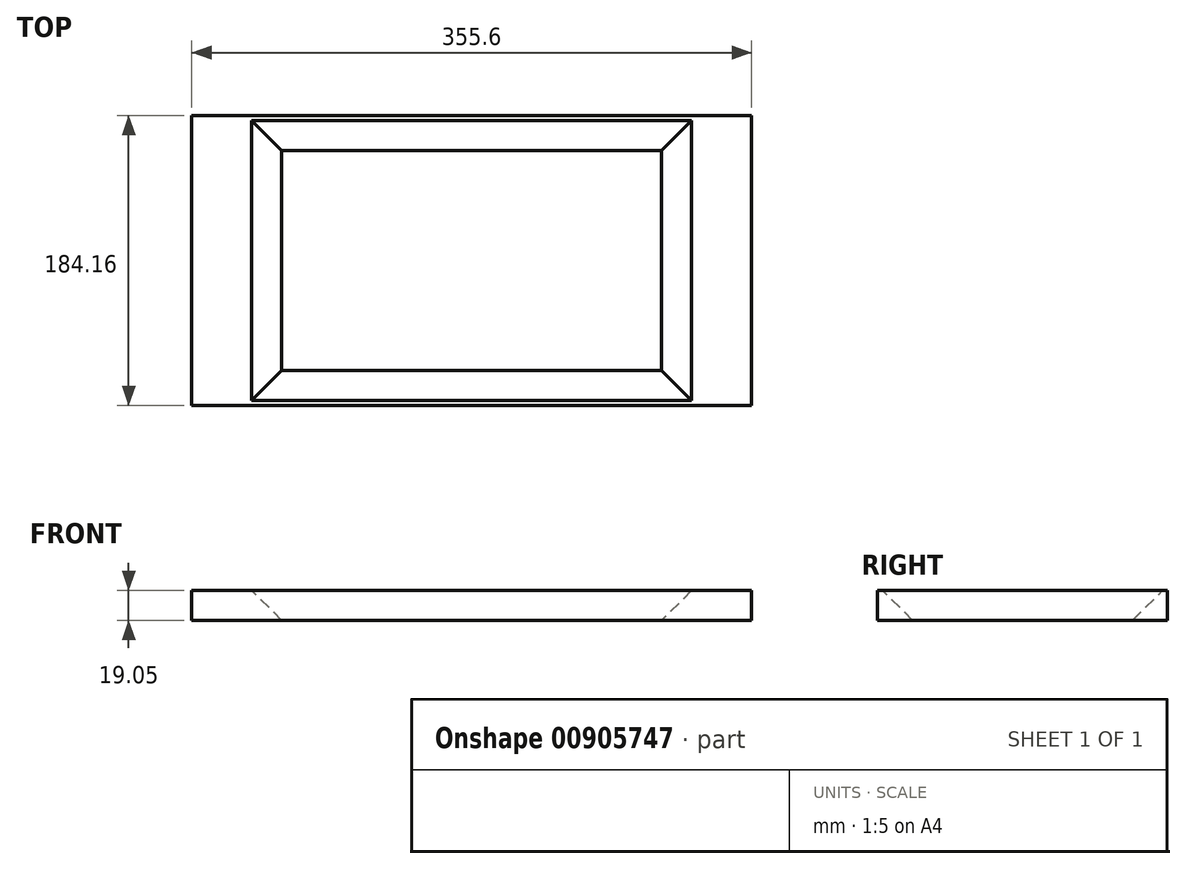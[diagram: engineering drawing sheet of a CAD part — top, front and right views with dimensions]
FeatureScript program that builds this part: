
annotation { "Feature Type Name" : "Feature", "Feature Type Description" : "" }
export const myFeature = defineFeature(function(context is Context, id is Id, definition is map)
    precondition{}
    {
        {
            var Q0;
            Q0=qCreatedBy(makeId("Top.planeOp"),FACE);
            var sketch = newSketch(context, id + "F0", { "sketchPlane" : qUnion([Q0])});
            skLineSegment(sketch, "E0.bottom", {"start": v(177.8, 92.08) * mm, "end": v(-177.8, 92.08) * mm});
            skLineSegment(sketch, "E0.top", {"start": v(177.8, -92.08) * mm, "end": v(-177.8, -92.08) * mm});
            skLineSegment(sketch, "E0.left", {"start": v(177.8, 92.08) * mm, "end": v(177.8, -92.08) * mm});
            skLineSegment(sketch, "E0.right", {"start": v(-177.8, 92.08) * mm, "end": v(-177.8, -92.08) * mm});
            skPoint(sketch, "E0.middle", {"position": v(0, 0) * mm});
            skLineSegment(sketch, "E1.bottom", {"start": v(120.65, 69.85) * mm, "end": v(-120.65, 69.85) * mm});
            skLineSegment(sketch, "E1.top", {"start": v(120.65, -69.85) * mm, "end": v(-120.65, -69.85) * mm});
            skLineSegment(sketch, "E1.left", {"start": v(120.65, 69.85) * mm, "end": v(120.65, -69.85) * mm});
            skLineSegment(sketch, "E1.right", {"start": v(-120.65, 69.85) * mm, "end": v(-120.65, -69.85) * mm});
            skSolve(sketch);
        }
        {
            var Q0;
            Q0 = qSketchRegion(id + "F0", true);
            extrude(context, id + "F1", {"entities" : qUnion([Q0]), "depth" : 19.05 * mm, "offsetDistance" : 25.4 * mm});
        }
        {
            var Q0;
            Q0=makeQuery(id+"F1.opExtrude","CAP_EDGE",EDGE,{"disambiguationData":[OSD([sQuery(id+"F0.wireOp",EDGE,"E1.right")])],"isStart":false});
            var Q1;
            Q1=makeQuery(id+"F1.opExtrude","CAP_EDGE",EDGE,{"disambiguationData":[OSD([sQuery(id+"F0.wireOp",EDGE,"E1.bottom")])],"isStart":false});
            var Q2;
            Q2=makeQuery(id+"F1.opExtrude","CAP_EDGE",EDGE,{"disambiguationData":[OSD([sQuery(id+"F0.wireOp",EDGE,"E1.left")])],"isStart":false});
            var Q3;
            Q3=makeQuery(id+"F1.opExtrude","CAP_EDGE",EDGE,{"disambiguationData":[OSD([sQuery(id+"F0.wireOp",EDGE,"E1.top")])],"isStart":false});
            chamfer(context, id + "F2", {"entities" : qUnion([Q0, Q1, Q2, Q3]), "width" : 19.05 * mm, "tangentPropagation" : true});
        }
    });
